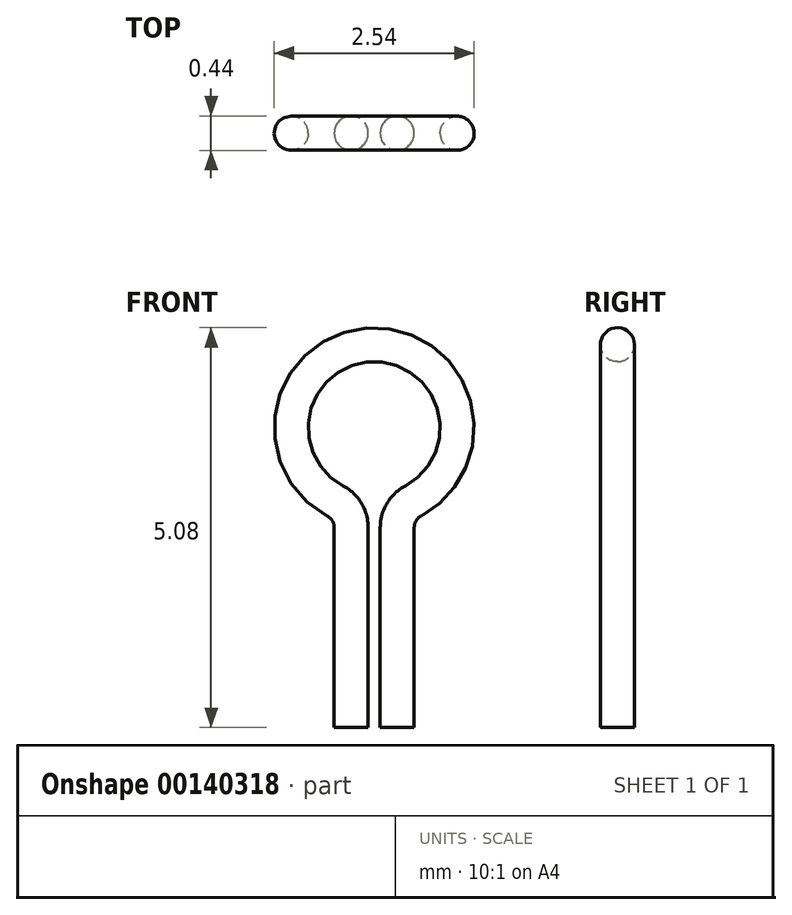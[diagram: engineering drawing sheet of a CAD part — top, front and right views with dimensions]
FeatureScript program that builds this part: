
annotation { "Feature Type Name" : "Feature", "Feature Type Description" : "" }
export const myFeature = defineFeature(function(context is Context, id is Id, definition is map)
    precondition{}
    {
        {
            var Q0;
            Q0=qCreatedBy(makeId("Front.planeOp"),FACE);
            var sketch = newSketch(context, id + "F0", { "sketchPlane" : qUnion([Q0])});
            skArc(sketch, "E0", {"start": v(0.5, 0.34) * mm, "mid": v(0, 2.32) * mm, "end": v(-0.5, 0.34) * mm});
            skLineSegment(sketch, "E1", {"start": v(-0.3, 0) * mm, "end": v(-0.3, -2.54) * mm});
            skLineSegment(sketch, "E2", {"start": v(0.3, 0) * mm, "end": v(0.3, -2.54) * mm});
            skLineSegment(sketch, "E3", {"start": v(0, 0.43) * mm, "end": v(0, 0) * mm, "construction": true});
            skPoint(sketch, "E4", {"position": v(0, 0.22) * mm});
            skLineSegment(sketch, "E5", {"start": v(-0.5, 0) * mm, "end": v(-0.08, 0) * mm, "construction": true});
            skLineSegment(sketch, "E6", {"start": v(0.08, 0) * mm, "end": v(0.5, 0) * mm, "construction": true});
            skPoint(sketch, "E7", {"position": v(0.3, 0) * mm});
            skPoint(sketch, "E8", {"position": v(-0.3, 0) * mm});
            skArc(sketch, "E9", {"start": v(-0.3, 0.26) * mm, "mid": v(0, 0.22) * mm, "end": v(0.3, 0.26) * mm, "construction": true});
            skArc(sketch, "E10", {"start": v(-0.3, 0) * mm, "mid": v(-0.35, 0.2) * mm, "end": v(-0.5, 0.34) * mm});
            skArc(sketch, "E11", {"start": v(0.5, 0.34) * mm, "mid": v(0.35, 0.2) * mm, "end": v(0.3, 0) * mm});
            skLineSegment(sketch, "E12", {"start": v(0, 2.54) * mm, "end": v(0, 2.1) * mm, "construction": true});
            skPoint(sketch, "E13", {"position": v(0, 2.32) * mm});
            skSolve(sketch);
        }
        {
            var Q0;
            Q0=sQuery(id+"F0.wireOp",VERTEX,"E2.end");
            var Q1;
            Q1=qCreatedBy(makeId("Top.planeOp"),FACE);
            cPlane(context, id + "F1", {"entities" : qUnion([Q0, Q1]), "cplaneType" : CPlaneType.PLANE_POINT, "offset" : 25.4 * mm, "width" : 152.4 * mm, "height" : 152.4 * mm});
        }
        {
            var Q0;
            Q0=qCreatedBy(id+"F1.planeOp",FACE);
            var sketch = newSketch(context, id + "F2", { "sketchPlane" : qUnion([Q0])});
            skCircle(sketch, "E14", {"center": v(-0.3, 0) * mm, "radius": 0.22 * mm});
            skSolve(sketch);
        }
        {
            var Q0;
            Q0 = qSketchRegion(id + "F2", true);
            var Q1;
            Q1 = qConstructionFilter(qBodyType(qCreatedBy(id + "F0" ,EDGE), BodyType.WIRE), ConstructionObject.NO);
            sweep(context, id + "F3", {"profiles" : qUnion([Q0]), "path" : qUnion([Q1])});
        }
    });
